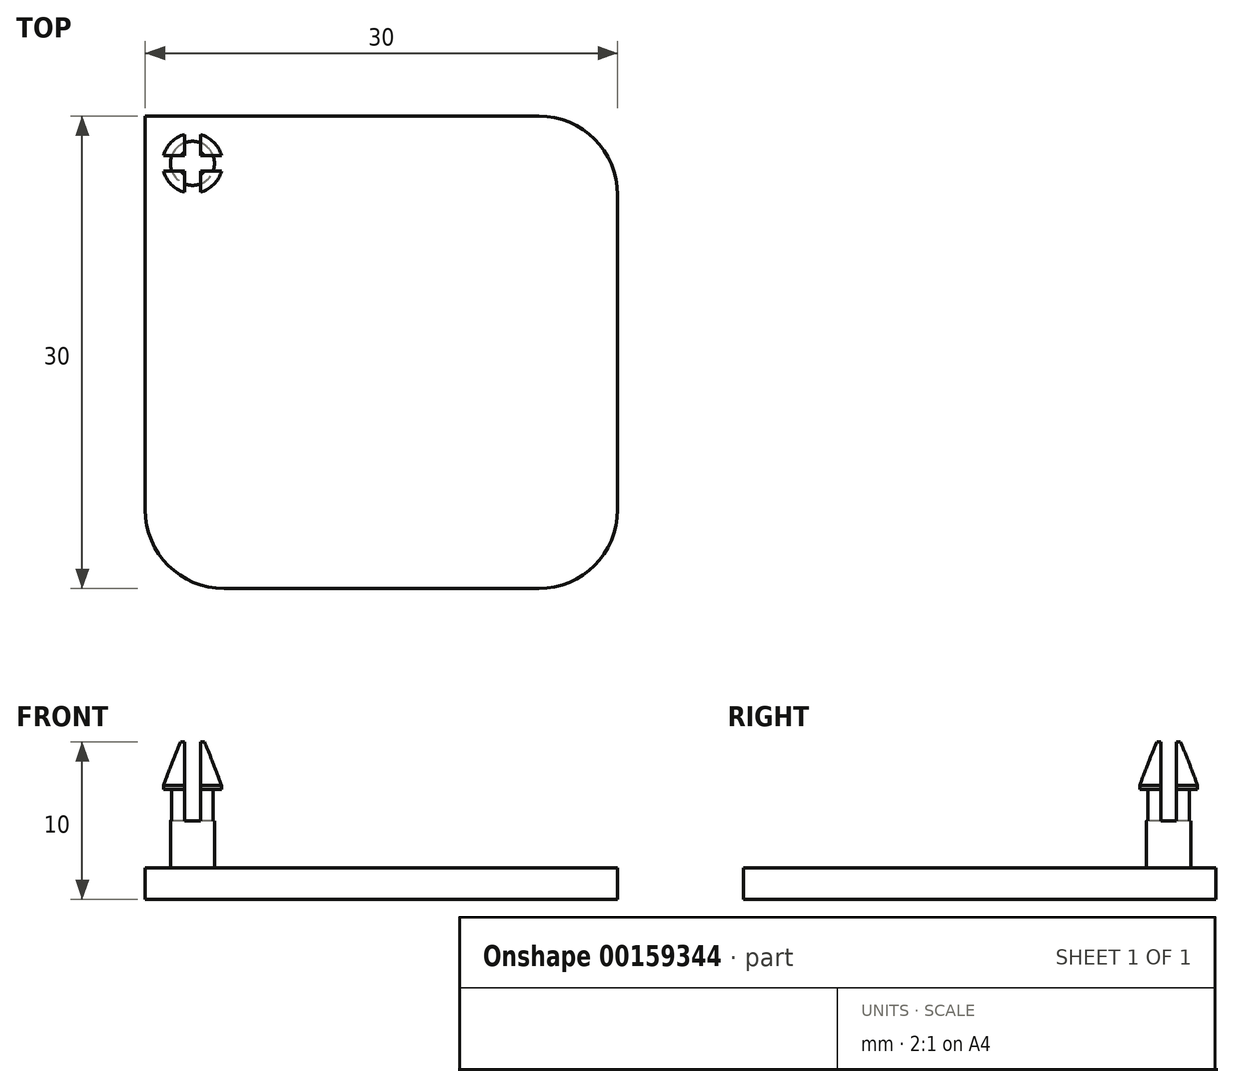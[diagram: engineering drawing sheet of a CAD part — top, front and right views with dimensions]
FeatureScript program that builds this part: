
annotation { "Feature Type Name" : "Feature", "Feature Type Description" : "" }
export const myFeature = defineFeature(function(context is Context, id is Id, definition is map)
    precondition{}
    {
        {
            var Q0;
            Q0=qCreatedBy(makeId("Top.planeOp"),FACE);
            var sketch = newSketch(context, id + "F0", { "sketchPlane" : qUnion([Q0])});
            skLineSegment(sketch, "E0.bottom", {"start": v(-15, 15) * mm, "end": v(15, 15) * mm});
            skLineSegment(sketch, "E0.top", {"start": v(-15, -15) * mm, "end": v(15, -15) * mm});
            skLineSegment(sketch, "E0.left", {"start": v(-15, 15) * mm, "end": v(-15, -15) * mm});
            skLineSegment(sketch, "E0.right", {"start": v(15, 15) * mm, "end": v(15, -15) * mm});
            skPoint(sketch, "E0.middle", {"position": v(0, 0) * mm});
            skSolve(sketch);
        }
        {
            var Q0;
            Q0 = qSketchRegion(id + "F0", true);
            extrude(context, id + "F1", {"entities" : qUnion([Q0]), "depth" : 2 * mm});
        }
        {
            var Q0;
            Q0=makeQuery(id+"F1.opExtrude","SWEPT_EDGE",EDGE,{"disambiguationData":[OSD([sQuery(id+"F0.wireOp",EDGE,"E0.top"),sQuery(id+"F0.wireOp",EDGE,"E0.left")])]});
            var Q1;
            Q1=makeQuery(id+"F1.opExtrude","SWEPT_EDGE",EDGE,{"disambiguationData":[OSD([sQuery(id+"F0.wireOp",EDGE,"E0.top"),sQuery(id+"F0.wireOp",EDGE,"E0.right")])]});
            var Q2;
            Q2=makeQuery(id+"F1.opExtrude","SWEPT_EDGE",EDGE,{"disambiguationData":[OSD([sQuery(id+"F0.wireOp",EDGE,"E0.bottom"),sQuery(id+"F0.wireOp",EDGE,"E0.right")])]});
            fillet(context, id + "F2", {"entities" : qUnion([Q0, Q1, Q2]), "radius" : 5 * mm, "tangentPropagation" : true, "allowEdgeOverflow" : false});
        }
        {
            var Q0;
            Q0=makeQuery(id+"F1.opExtrude","CAP_FACE",FACE,{"disambiguationData":[OSD([sQuery(id+"F0.wireOp",EDGE,"E0.bottom"),sQuery(id+"F0.wireOp",EDGE,"E0.top"),sQuery(id+"F0.wireOp",EDGE,"E0.left"),sQuery(id+"F0.wireOp",EDGE,"E0.right")])],"isStart":false});
            var sketch = newSketch(context, id + "F3", { "sketchPlane" : qUnion([Q0])});
            skCircle(sketch, "E1", {"center": v(-12, 12) * mm, "radius": 1.4 * mm});
            skSolve(sketch);
        }
        {
            var Q0;
            Q0 = qSketchRegion(id + "F3", true);
            extrude(context, id + "F4", {"entities" : qUnion([Q0]), "operationType" : NewBodyOperationType.ADD, "depth" : 5 * mm});
        }
        {
            var Q0;
            Q0=makeQuery(id+"F4.opExtrude","CAP_FACE",FACE,{"disambiguationData":[OSD([sQuery(id+"F3.wireOp",EDGE,"E1")])],"isStart":false});
            var sketch = newSketch(context, id + "F5", { "sketchPlane" : qUnion([Q0])});
            skCircle(sketch, "E2", {"center": v(-12, 12) * mm, "radius": 1.9 * mm});
            skSolve(sketch);
        }
        {
            var Q0;
            Q0 = qSketchRegion(id + "F5", true);
            extrude(context, id + "F6", {"entities" : qUnion([Q0]), "operationType" : NewBodyOperationType.ADD, "depth" : 3 * mm});
        }
        {
            var Q0;
            Q0=makeQuery(id+"F6.opExtrude","CAP_FACE",FACE,{"disambiguationData":[OSD([sQuery(id+"F5.wireOp",EDGE,"E2")])],"isStart":false});
            var sketch = newSketch(context, id + "F7", { "sketchPlane" : qUnion([Q0])});
            skLineSegment(sketch, "E3.bottom", {"start": v(-9.9, 11.52) * mm, "end": v(-13.84, 11.52) * mm});
            skLineSegment(sketch, "E3.top", {"start": v(-10.16, 12.48) * mm, "end": v(-14.1, 12.48) * mm});
            skLineSegment(sketch, "E3.left", {"start": v(-9.9, 11.52) * mm, "end": v(-10.16, 12.48) * mm});
            skLineSegment(sketch, "E3.right", {"start": v(-13.84, 11.52) * mm, "end": v(-14.1, 12.48) * mm});
            skPoint(sketch, "E3.middle", {"position": v(-12, 12) * mm});
            skLineSegment(sketch, "E4.bottom", {"start": v(-11.5, 13.9) * mm, "end": v(-12.5, 13.9) * mm});
            skLineSegment(sketch, "E4.top", {"start": v(-11.5, 10.1) * mm, "end": v(-12.5, 10.1) * mm});
            skLineSegment(sketch, "E4.left", {"start": v(-11.5, 13.9) * mm, "end": v(-11.5, 10.1) * mm});
            skLineSegment(sketch, "E4.right", {"start": v(-12.5, 13.9) * mm, "end": v(-12.5, 10.1) * mm});
            skSolve(sketch);
        }
        {
            var Q0;
            Q0 = qSketchRegion(id + "F7", true);
            extrude(context, id + "F8", {"entities" : qUnion([Q0]), "operationType" : NewBodyOperationType.REMOVE, "oppositeDirection" : true, "depth" : 5 * mm});
        }
        {
            var Q0;
            {var subQ0=sQuery(id+"F5.wireOp",EDGE,"E2");var subQ1=sQuery(id+"F7.wireOp",EDGE,"E4.left");var subQ2=sQuery(id+"F7.wireOp",EDGE,"E3.bottom");var subQ3=makeQuery(id+"F7.imprint","INTERSECT",VERTEX,{"derivedFrom":[subQ2,subQ1]});var subQ4=makeQuery(id+"F6.opExtrude","CAP_EDGE",EDGE,{"disambiguationData":[OSD([subQ0])],"isStart":false});Q0=makeQuery(id+"F8.boolean.opBoolean","SPLIT",EDGE,{"disambiguationData":[TD([makeQuery(id+"F8.opExtrude","SWEPT_FACE",FACE,{"disambiguationData":[OSD([subQ2]),TDD([makeQuery(id+"F7.imprint","IMPRINT",EDGE,{"disambiguationData":[TD([[makeQuery(id+"F7.imprint","INTERSECT",VERTEX,{"derivedFrom":[subQ2,sQuery(id+"F7.wireOp",EDGE,"E3.left")]}),-1.0]])],"derivedFrom":subQ2}),makeQuery(id+"F7.imprint","IMPRINT",EDGE,{"disambiguationData":[TD([[subQ3,1.0]])],"derivedFrom":subQ2})])]})])],"derivedFrom":subQ4});}
            var Q1;
            {var subQ0=sQuery(id+"F5.wireOp",EDGE,"E2");var subQ1=sQuery(id+"F7.wireOp",EDGE,"E3.top");var subQ2=makeQuery(id+"F6.opExtrude","CAP_EDGE",EDGE,{"disambiguationData":[OSD([subQ0])],"isStart":false});var subQ3=sQuery(id+"F7.wireOp",EDGE,"E4.left");var subQ4=makeQuery(id+"F7.imprint","INTERSECT",VERTEX,{"derivedFrom":[subQ1,subQ3]});Q1=makeQuery(id+"F8.boolean.opBoolean","SPLIT",EDGE,{"disambiguationData":[TD([makeQuery(id+"F8.opExtrude","SWEPT_FACE",FACE,{"disambiguationData":[OSD([subQ1]),TDD([makeQuery(id+"F7.imprint","IMPRINT",EDGE,{"disambiguationData":[TD([[subQ4,1.0]])],"derivedFrom":subQ1})])]})])],"derivedFrom":subQ2});}
            var Q2;
            {var subQ0=sQuery(id+"F5.wireOp",EDGE,"E2");var subQ1=sQuery(id+"F7.wireOp",EDGE,"E4.right");var subQ2=sQuery(id+"F7.wireOp",EDGE,"E3.top");var subQ3=makeQuery(id+"F7.imprint","INTERSECT",VERTEX,{"derivedFrom":[subQ2,subQ1]});var subQ4=makeQuery(id+"F6.opExtrude","CAP_EDGE",EDGE,{"disambiguationData":[OSD([subQ0])],"isStart":false});Q2=makeQuery(id+"F8.boolean.opBoolean","SPLIT",EDGE,{"disambiguationData":[TD([makeQuery(id+"F8.opExtrude","SWEPT_FACE",FACE,{"disambiguationData":[OSD([subQ2]),TDD([makeQuery(id+"F7.imprint","IMPRINT",EDGE,{"disambiguationData":[TD([[subQ3,-1.0]])],"derivedFrom":subQ2}),makeQuery(id+"F7.imprint","IMPRINT",EDGE,{"disambiguationData":[TD([[makeQuery(id+"F7.imprint","INTERSECT",VERTEX,{"derivedFrom":[subQ2,sQuery(id+"F7.wireOp",EDGE,"E3.right")]}),1.0]])],"derivedFrom":subQ2})])]})])],"derivedFrom":subQ4});}
            var Q3;
            {var subQ0=sQuery(id+"F5.wireOp",EDGE,"E2");var subQ1=sQuery(id+"F7.wireOp",EDGE,"E4.right");var subQ2=makeQuery(id+"F6.opExtrude","CAP_EDGE",EDGE,{"disambiguationData":[OSD([subQ0])],"isStart":false});var subQ4=sQuery(id+"F7.wireOp",EDGE,"E3.bottom");var subQ5=makeQuery(id+"F7.imprint","INTERSECT",VERTEX,{"derivedFrom":[subQ4,subQ1]});Q3=makeQuery(id+"F8.boolean.opBoolean","SPLIT",EDGE,{"disambiguationData":[TD([makeQuery(id+"F8.opExtrude","SWEPT_FACE",FACE,{"disambiguationData":[OSD([subQ4]),TDD([makeQuery(id+"F7.imprint","IMPRINT",EDGE,{"disambiguationData":[TD([[subQ5,-1.0]])],"derivedFrom":subQ4})])]})])],"derivedFrom":subQ2});}
            chamfer(context, id + "F9", {"entities" : qUnion([Q0, Q1, Q2, Q3]), "chamferType" : ChamferType.OFFSET_ANGLE, "width" : 1 * mm, "oppositeDirection" : false, "angle" : 70 * degree, "tangentPropagation" : true});
        }
    });
